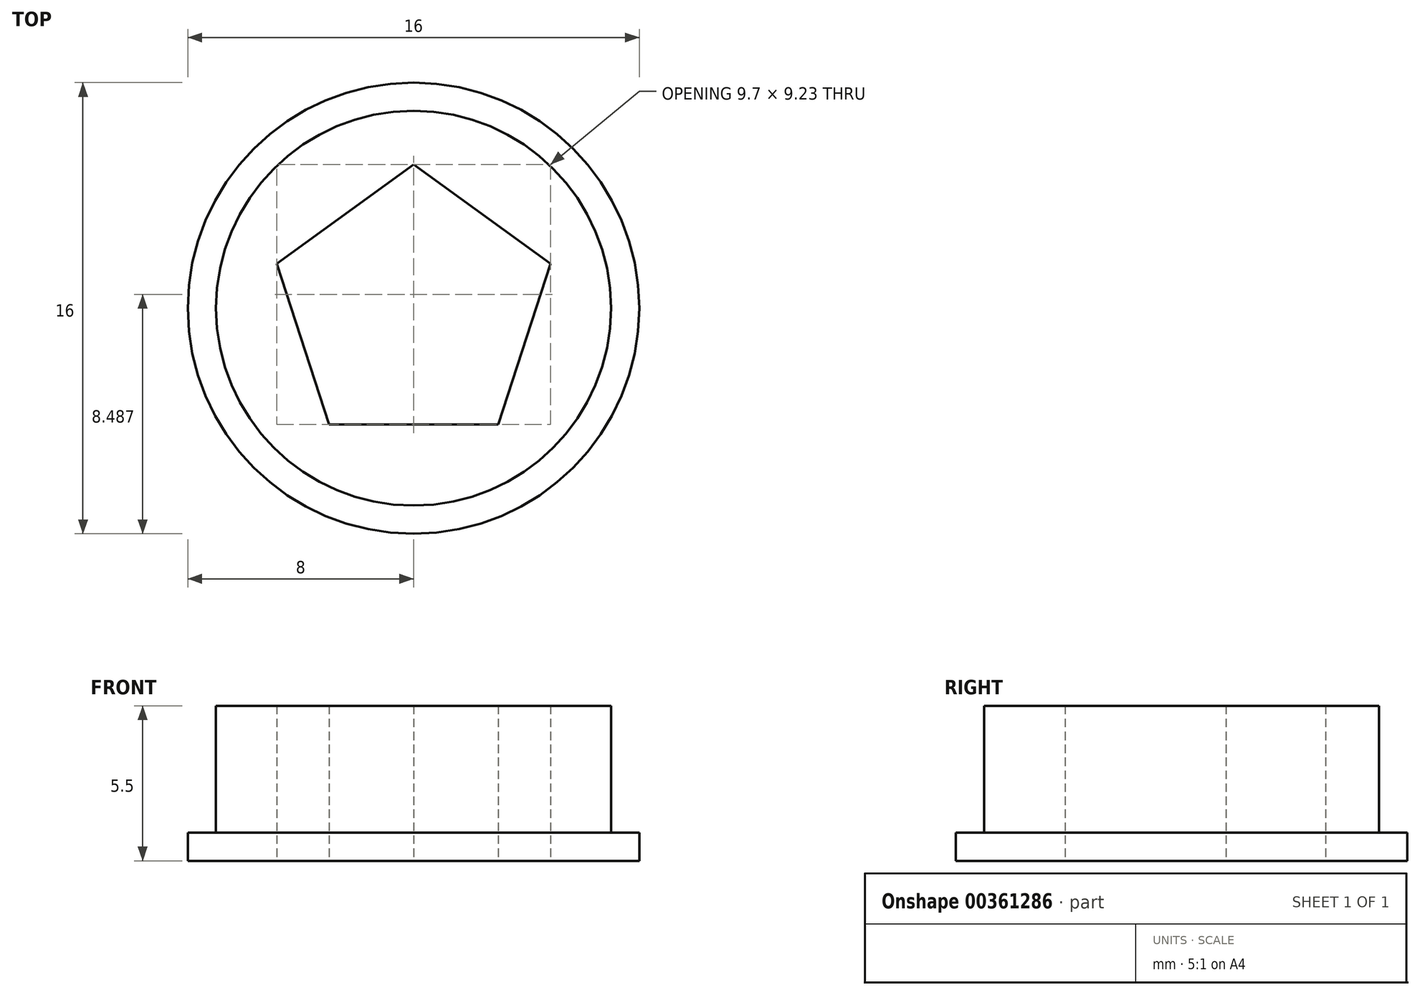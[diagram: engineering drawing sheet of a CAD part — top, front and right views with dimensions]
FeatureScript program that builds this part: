
annotation { "Feature Type Name" : "Feature", "Feature Type Description" : "" }
export const myFeature = defineFeature(function(context is Context, id is Id, definition is map)
    precondition{}
    {
        {
            var Q0;
            Q0=qCreatedBy(makeId("Top.planeOp"),FACE);
            var sketch = newSketch(context, id + "F0", { "sketchPlane" : qUnion([Q0])});
            skCircle(sketch, "E0.cCircle", {"center": v(0, 0) * mm, "radius": 4.13 * mm, "construction": true});
            skLineSegment(sketch, "E0.0", {"start": v(4.85, 1.58) * mm, "end": v(3, -4.13) * mm});
            skLineSegment(sketch, "E0.1", {"start": v(3, -4.13) * mm, "end": v(-3, -4.13) * mm});
            skLineSegment(sketch, "E0.2", {"start": v(-3, -4.13) * mm, "end": v(-4.85, 1.58) * mm});
            skLineSegment(sketch, "E0.3", {"start": v(-4.85, 1.58) * mm, "end": v(0, 5.1) * mm});
            skLineSegment(sketch, "E0.4", {"start": v(0, 5.1) * mm, "end": v(4.85, 1.58) * mm});
            skPoint(sketch, "E0.0.midPoint", {"position": v(3.92, -1.27) * mm});
            skCircle(sketch, "E1", {"center": v(0, 0) * mm, "radius": 7 * mm});
            skCircle(sketch, "E2", {"center": v(0, 0) * mm, "radius": 8 * mm});
            skSolve(sketch);
        }
        {
            var Q0;
            Q0=makeQuery(id+"F0.imprint","IMPRINT",FACE,{"disambiguationData":[TD([[makeQuery(id+"F0.imprint","IMPRINT",EDGE,{"derivedFrom":sQuery(id+"F0.wireOp",EDGE,"E0.0")}),1.0]])]});
            extrude(context, id + "F1", {"entities" : qUnion([Q0]), "depth" : 5.5 * mm});
        }
        {
            var Q0;
            Q0=makeQuery(id+"F0.imprint","IMPRINT",FACE,{"disambiguationData":[TD([[makeQuery(id+"F0.imprint","IMPRINT",EDGE,{"derivedFrom":sQuery(id+"F0.wireOp",EDGE,"E1")}),-1.0]])]});
            extrude(context, id + "F2", {"entities" : qUnion([Q0]), "operationType" : NewBodyOperationType.ADD, "depth" : 1 * mm});
        }
    });
